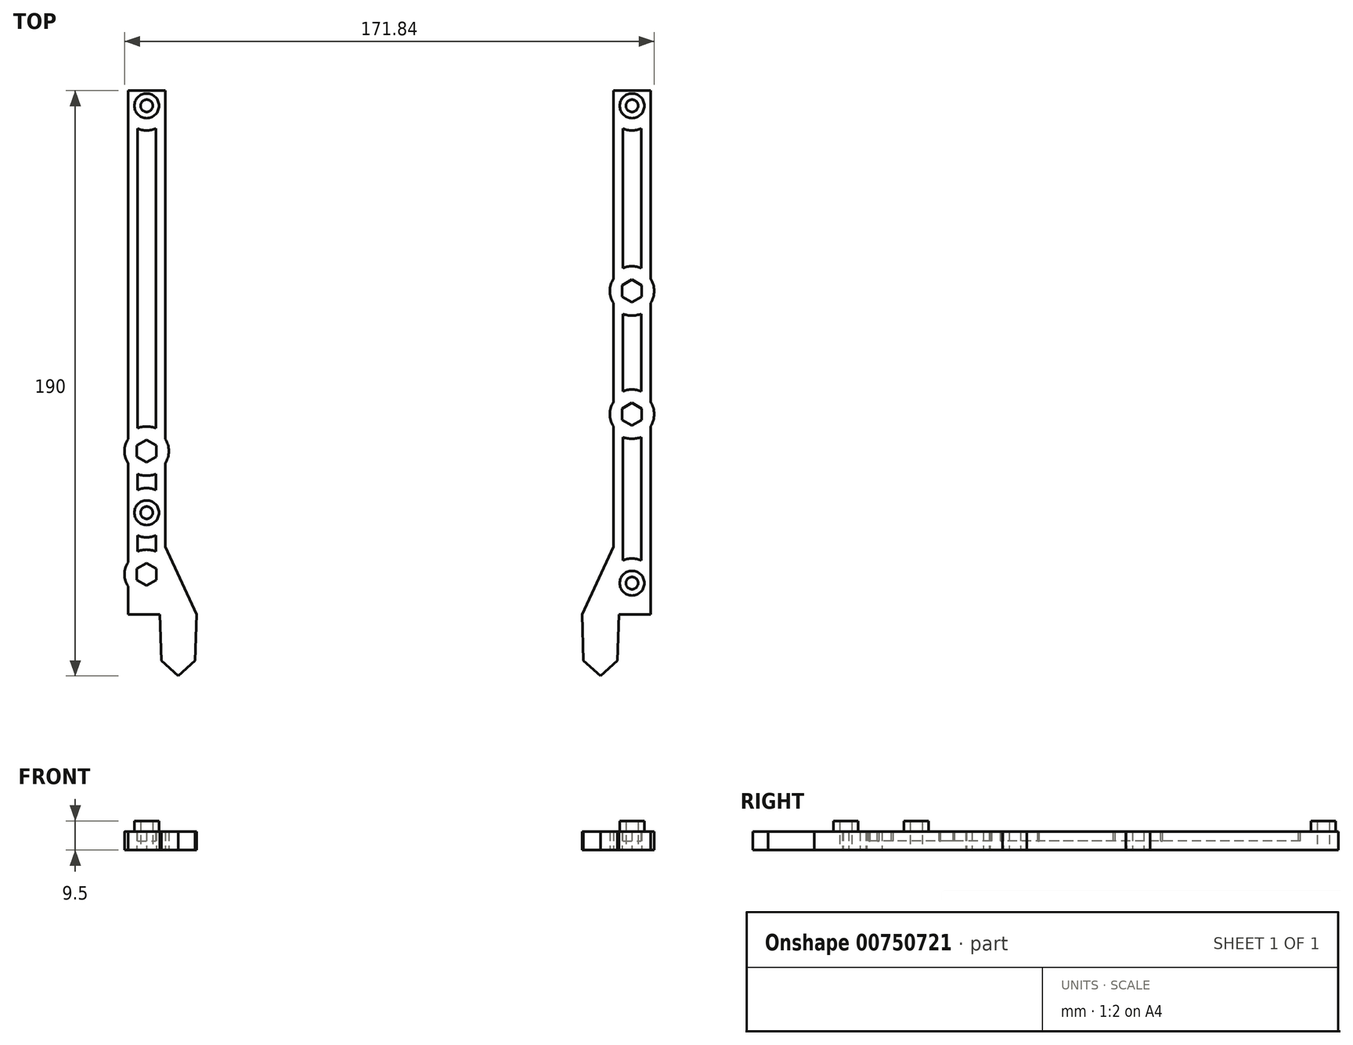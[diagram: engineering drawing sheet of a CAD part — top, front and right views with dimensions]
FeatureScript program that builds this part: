
annotation { "Feature Type Name" : "Feature", "Feature Type Description" : "" }
export const myFeature = defineFeature(function(context is Context, id is Id, definition is map)
    precondition{}
    {
        {
            var Q0;
            Q0=qCreatedBy(makeId("Top.planeOp"),FACE);
            var sketch = newSketch(context, id + "F0", { "sketchPlane" : qUnion([Q0])});
            skLineSegment(sketch, "E0", {"start": v(-84.74, -85) * mm, "end": v(-84.74, 85) * mm});
            skLineSegment(sketch, "E1", {"start": v(-84.74, 85) * mm, "end": v(-72.74, 85) * mm});
            skLineSegment(sketch, "E2", {"start": v(-72.74, 85) * mm, "end": v(-72.74, -63.04) * mm});
            skLineSegment(sketch, "E3", {"start": v(-74.5, -85) * mm, "end": v(-84.74, -85) * mm});
            skLineSegment(sketch, "E4", {"start": v(-74.5, -85) * mm, "end": v(-62.5, -85) * mm, "construction": true});
            skLineSegment(sketch, "E5", {"start": v(-72.74, -63.04) * mm, "end": v(-62.5, -85) * mm});
            skLineSegment(sketch, "E6", {"start": v(-74.5, -85) * mm, "end": v(-74, -100) * mm});
            skLineSegment(sketch, "E7", {"start": v(-74, -100) * mm, "end": v(-68.5, -105) * mm});
            skLineSegment(sketch, "E8", {"start": v(-68.5, -105) * mm, "end": v(-63, -100) * mm});
            skLineSegment(sketch, "E9", {"start": v(-63, -100) * mm, "end": v(-62.5, -85) * mm});
            skLineSegment(sketch, "E10", {"start": v(-78.74, 85) * mm, "end": v(-78.74, -85) * mm, "construction": true});
            skLineSegment(sketch, "E11.MirrorCS", {"start": v(68.5, -105) * mm, "end": v(63, -100) * mm});
            skLineSegment(sketch, "E12.MirrorCS", {"start": v(74, -100) * mm, "end": v(68.5, -105) * mm});
            skLineSegment(sketch, "E13.MirrorCS", {"start": v(74.5, -85) * mm, "end": v(84.74, -85) * mm});
            skLineSegment(sketch, "E14.MirrorCS", {"start": v(84.74, 85) * mm, "end": v(72.74, 85) * mm});
            skLineSegment(sketch, "E15.MirrorCS", {"start": v(74.5, -85) * mm, "end": v(74, -100) * mm});
            skLineSegment(sketch, "E16.MirrorCS", {"start": v(78.74, 85) * mm, "end": v(78.74, -85) * mm, "construction": true});
            skLineSegment(sketch, "E17.MirrorCS", {"start": v(84.74, -85) * mm, "end": v(84.74, 85) * mm});
            skLineSegment(sketch, "E18.MirrorCS", {"start": v(72.74, -63.04) * mm, "end": v(62.5, -85) * mm});
            skLineSegment(sketch, "E19.MirrorCS", {"start": v(74.5, -85) * mm, "end": v(62.5, -85) * mm, "construction": true});
            skLineSegment(sketch, "E20.MirrorCS", {"start": v(72.74, 85) * mm, "end": v(72.74, -63.04) * mm});
            skLineSegment(sketch, "E21.MirrorCS", {"start": v(63, -100) * mm, "end": v(62.5, -85) * mm});
            skCircle(sketch, "E22", {"center": v(-78.74, 80.1) * mm, "radius": 2 * mm});
            skCircle(sketch, "E23", {"center": v(-78.74, -51.98) * mm, "radius": 2 * mm});
            skCircle(sketch, "E24", {"center": v(78.74, 80.1) * mm, "radius": 2 * mm});
            skCircle(sketch, "E25", {"center": v(78.74, -74.84) * mm, "radius": 2 * mm});
            skLineSegment(sketch, "E26", {"start": v(-78.74, 80.1) * mm, "end": v(78.74, 80.1) * mm, "construction": true});
            skLineSegment(sketch, "E27", {"start": v(-78.74, 0) * mm, "end": v(78.74, 0) * mm, "construction": true});
            skPoint(sketch, "E28", {"position": v(0, 0) * mm});
            skLineSegment(sketch, "E29", {"start": v(-68.5, -85) * mm, "end": v(68.5, -85) * mm, "construction": true});
            skSolve(sketch);
        }
        {
            var Q0;
            Q0 = qSketchRegion(id + "F0", true);
            extrude(context, id + "F1", {"entities" : qUnion([Q0]), "depth" : 6 * mm, "offsetDistance" : 25 * mm});
        }
        {
            var Q0;
            Q0=qCreatedBy(makeId("Top.planeOp"),FACE);
            var sketch = newSketch(context, id + "F2", { "sketchPlane" : qUnion([Q0])});
            skCircle(sketch, "E30.0", {"center": v(-78.74, -51.98) * mm, "radius": 2 * mm});
            skCircle(sketch, "E30.1", {"center": v(78.74, -74.84) * mm, "radius": 2 * mm});
            skCircle(sketch, "E30.2", {"center": v(78.74, 80.1) * mm, "radius": 2 * mm});
            skCircle(sketch, "E30.3", {"center": v(-78.74, 80.1) * mm, "radius": 2 * mm});
            skCircle(sketch, "E31", {"center": v(-78.74, -51.98) * mm, "radius": 4 * mm});
            skCircle(sketch, "E32", {"center": v(-78.74, 80.1) * mm, "radius": 4 * mm});
            skCircle(sketch, "E33", {"center": v(78.74, -74.84) * mm, "radius": 4 * mm});
            skCircle(sketch, "E34", {"center": v(78.74, 80.1) * mm, "radius": 4 * mm});
            skSolve(sketch);
        }
        {
            var Q0;
            Q0 = qSketchRegion(id + "F2", true);
            extrude(context, id + "F3", {"entities" : qUnion([Q0]), "operationType" : NewBodyOperationType.ADD, "depth" : 9.5 * mm, "offsetDistance" : 25 * mm});
        }
        {
            var Q0;
            Q0=qCreatedBy(makeId("Top.planeOp"),FACE);
            var sketch = newSketch(context, id + "F4", { "sketchPlane" : qUnion([Q0])});
            skLineSegment(sketch, "E35", {"start": v(-78.74, -31.98) * mm, "end": v(-78.74, -71.98) * mm, "construction": true});
            skLineSegment(sketch, "E36", {"start": v(78.74, 20) * mm, "end": v(78.74, -20) * mm, "construction": true});
            skPoint(sketch, "E37", {"position": v(-78.74, -51.98) * mm});
            skPoint(sketch, "E38", {"position": v(78.74, 0) * mm});
            skCircle(sketch, "E39", {"center": v(-78.74, -31.98) * mm, "radius": 7.17 * mm});
            skCircle(sketch, "E40", {"center": v(-78.74, -71.98) * mm, "radius": 7.17 * mm});
            skCircle(sketch, "E41", {"center": v(78.74, 20) * mm, "radius": 7.17 * mm});
            skCircle(sketch, "E42", {"center": v(78.74, -20) * mm, "radius": 7.17 * mm});
            skCircle(sketch, "E43.cCircle", {"center": v(78.74, 20) * mm, "radius": 3.17 * mm, "construction": true});
            skLineSegment(sketch, "E43.0", {"start": v(81.92, 21.83) * mm, "end": v(81.92, 18.17) * mm});
            skLineSegment(sketch, "E43.1", {"start": v(81.92, 18.17) * mm, "end": v(78.74, 16.33) * mm});
            skLineSegment(sketch, "E43.2", {"start": v(78.74, 16.33) * mm, "end": v(75.57, 18.17) * mm});
            skLineSegment(sketch, "E43.3", {"start": v(75.56, 18.17) * mm, "end": v(75.56, 21.83) * mm});
            skLineSegment(sketch, "E43.4", {"start": v(75.56, 21.83) * mm, "end": v(78.74, 23.67) * mm});
            skLineSegment(sketch, "E43.5", {"start": v(78.74, 23.67) * mm, "end": v(81.92, 21.83) * mm});
            skPoint(sketch, "E43.0.midPoint", {"position": v(81.92, 20) * mm});
            skCircle(sketch, "E44.cCircle", {"center": v(78.74, -20) * mm, "radius": 3.17 * mm, "construction": true});
            skLineSegment(sketch, "E44.0", {"start": v(81.91, -18.17) * mm, "end": v(81.91, -21.83) * mm});
            skLineSegment(sketch, "E44.1", {"start": v(81.91, -21.83) * mm, "end": v(78.74, -23.67) * mm});
            skLineSegment(sketch, "E44.2", {"start": v(78.74, -23.67) * mm, "end": v(75.56, -21.83) * mm});
            skLineSegment(sketch, "E44.3", {"start": v(75.56, -21.83) * mm, "end": v(75.56, -18.17) * mm});
            skLineSegment(sketch, "E44.4", {"start": v(75.56, -18.17) * mm, "end": v(78.74, -16.33) * mm});
            skLineSegment(sketch, "E44.5", {"start": v(78.74, -16.33) * mm, "end": v(81.91, -18.17) * mm});
            skPoint(sketch, "E44.0.midPoint", {"position": v(81.91, -20) * mm});
            skCircle(sketch, "E45.cCircle", {"center": v(-78.74, -31.98) * mm, "radius": 3.17 * mm, "construction": true});
            skLineSegment(sketch, "E45.0", {"start": v(-75.57, -30.15) * mm, "end": v(-75.57, -33.81) * mm});
            skLineSegment(sketch, "E45.1", {"start": v(-75.57, -33.81) * mm, "end": v(-78.74, -35.65) * mm});
            skLineSegment(sketch, "E45.2", {"start": v(-78.74, -35.65) * mm, "end": v(-81.92, -33.81) * mm});
            skLineSegment(sketch, "E45.3", {"start": v(-81.92, -33.81) * mm, "end": v(-81.92, -30.15) * mm});
            skLineSegment(sketch, "E45.4", {"start": v(-81.92, -30.15) * mm, "end": v(-78.74, -28.31) * mm});
            skLineSegment(sketch, "E45.5", {"start": v(-78.74, -28.31) * mm, "end": v(-75.57, -30.15) * mm});
            skPoint(sketch, "E45.0.midPoint", {"position": v(-75.57, -31.98) * mm});
            skCircle(sketch, "E46.cCircle", {"center": v(-78.74, -71.98) * mm, "radius": 3.17 * mm, "construction": true});
            skLineSegment(sketch, "E46.0", {"start": v(-75.57, -70.15) * mm, "end": v(-75.57, -73.81) * mm});
            skLineSegment(sketch, "E46.1", {"start": v(-75.57, -73.81) * mm, "end": v(-78.74, -75.65) * mm});
            skLineSegment(sketch, "E46.2", {"start": v(-78.74, -75.65) * mm, "end": v(-81.92, -73.81) * mm});
            skLineSegment(sketch, "E46.3", {"start": v(-81.92, -73.81) * mm, "end": v(-81.92, -70.15) * mm});
            skLineSegment(sketch, "E46.4", {"start": v(-81.92, -70.15) * mm, "end": v(-78.74, -68.31) * mm});
            skLineSegment(sketch, "E46.5", {"start": v(-78.74, -68.31) * mm, "end": v(-75.57, -70.15) * mm});
            skPoint(sketch, "E46.0.midPoint", {"position": v(-75.57, -71.98) * mm});
            skCircle(sketch, "E47.0", {"center": v(-78.74, -51.98) * mm, "radius": 2 * mm, "construction": true});
            skLineSegment(sketch, "E48.0", {"start": v(78.74, 85) * mm, "end": v(78.74, -85) * mm, "construction": true});
            skSolve(sketch);
        }
        {
            var Q0;
            Q0 = qSketchRegion(id + "F4", true);
            var Q1;
            Q1=makeQuery(id+"F1.opExtrude","CAP_FACE",FACE,{"disambiguationData":[OSD([sQuery(id+"F0.wireOp",EDGE,"E0"),sQuery(id+"F0.wireOp",EDGE,"E1"),sQuery(id+"F0.wireOp",EDGE,"E2"),sQuery(id+"F0.wireOp",EDGE,"E3"),sQuery(id+"F0.wireOp",EDGE,"E5"),sQuery(id+"F0.wireOp",EDGE,"E6"),sQuery(id+"F0.wireOp",EDGE,"E7"),sQuery(id+"F0.wireOp",EDGE,"E8"),sQuery(id+"F0.wireOp",EDGE,"E9"),sQuery(id+"F0.wireOp",EDGE,"E22"),sQuery(id+"F0.wireOp",EDGE,"E23")])],"isStart":false});
            extrude(context, id + "F5", {"entities" : qUnion([Q0]), "operationType" : NewBodyOperationType.ADD, "endBound" : BoundingType.UP_TO_SURFACE, "depth" : 25 * mm, "endBoundEntityFace" : qUnion([Q1]), "offsetDistance" : 25 * mm});
        }
        {
            var Q0;
            Q0=makeQuery(id+"F4.imprint","IMPRINT",FACE,{"disambiguationData":[TD([[makeQuery(id+"F4.imprint","IMPRINT",EDGE,{"derivedFrom":sQuery(id+"F4.wireOp",EDGE,"E45.0")}),-1.0]])]});
            var Q1;
            Q1=makeQuery(id+"F4.imprint","IMPRINT",FACE,{"disambiguationData":[TD([[makeQuery(id+"F4.imprint","IMPRINT",EDGE,{"derivedFrom":sQuery(id+"F4.wireOp",EDGE,"E46.0")}),-1.0]])]});
            var Q2;
            Q2=makeQuery(id+"F4.imprint","IMPRINT",FACE,{"disambiguationData":[TD([[makeQuery(id+"F4.imprint","IMPRINT",EDGE,{"derivedFrom":sQuery(id+"F4.wireOp",EDGE,"E44.0")}),-1.0]])]});
            var Q3;
            Q3=makeQuery(id+"F4.imprint","IMPRINT",FACE,{"disambiguationData":[TD([[makeQuery(id+"F4.imprint","IMPRINT",EDGE,{"derivedFrom":sQuery(id+"F4.wireOp",EDGE,"E43.0")}),-1.0]])]});
            extrude(context, id + "F6", {"entities" : qUnion([Q0, Q1, Q2, Q3]), "operationType" : NewBodyOperationType.REMOVE, "endBound" : BoundingType.THROUGH_ALL, "depth" : 25 * mm, "offsetDistance" : 25 * mm});
        }
        {
            var Q0;
            Q0=makeQuery(id+"F5.boolean.opBoolean","MERGE",FACE,{"derivedFrom":[makeQuery(id+"F1.opExtrude","CAP_FACE",FACE,{"disambiguationData":[OSD([sQuery(id+"F0.wireOp",EDGE,"E0"),sQuery(id+"F0.wireOp",EDGE,"E1"),sQuery(id+"F0.wireOp",EDGE,"E2"),sQuery(id+"F0.wireOp",EDGE,"E3"),sQuery(id+"F0.wireOp",EDGE,"E5"),sQuery(id+"F0.wireOp",EDGE,"E6"),sQuery(id+"F0.wireOp",EDGE,"E7"),sQuery(id+"F0.wireOp",EDGE,"E8"),sQuery(id+"F0.wireOp",EDGE,"E9"),sQuery(id+"F0.wireOp",EDGE,"E22"),sQuery(id+"F0.wireOp",EDGE,"E23")])],"isStart":false}),makeQuery(id+"F5.opExtrude","CAP_FACE",FACE,{"disambiguationData":[OSD([sQuery(id+"F4.wireOp",EDGE,"SRqQKz3n-vC3j-pEua-mdw7-BWJlVyXjlK89"),sQuery(id+"F4.wireOp",EDGE,"6ef7abd1-16c0-451d-831a-03148b24f05d.0"),sQuery(id+"F4.wireOp",EDGE,"6ef7abd1-16c0-451d-831a-03148b24f05d.1"),sQuery(id+"F4.wireOp",EDGE,"6ef7abd1-16c0-451d-831a-03148b24f05d.2"),sQuery(id+"F4.wireOp",EDGE,"6ef7abd1-16c0-451d-831a-03148b24f05d.3"),sQuery(id+"F4.wireOp",EDGE,"6ef7abd1-16c0-451d-831a-03148b24f05d.4"),sQuery(id+"F4.wireOp",EDGE,"6ef7abd1-16c0-451d-831a-03148b24f05d.5")])],"isStart":false}),makeQuery(id+"F5.opExtrude","CAP_FACE",FACE,{"disambiguationData":[OSD([sQuery(id+"F4.wireOp",EDGE,"ubodkBIp-3K7r-hwd0-fg8X-iVVL0fXusPFp"),sQuery(id+"F4.wireOp",EDGE,"432d3784-bb52-43d7-afc3-5c8ebb29258b.0"),sQuery(id+"F4.wireOp",EDGE,"432d3784-bb52-43d7-afc3-5c8ebb29258b.1"),sQuery(id+"F4.wireOp",EDGE,"432d3784-bb52-43d7-afc3-5c8ebb29258b.2"),sQuery(id+"F4.wireOp",EDGE,"432d3784-bb52-43d7-afc3-5c8ebb29258b.3"),sQuery(id+"F4.wireOp",EDGE,"432d3784-bb52-43d7-afc3-5c8ebb29258b.4"),sQuery(id+"F4.wireOp",EDGE,"432d3784-bb52-43d7-afc3-5c8ebb29258b.5")])],"isStart":false})]});
            var sketch = newSketch(context, id + "F7", { "sketchPlane" : qUnion([Q0])});
            skCircle(sketch, "E49.0", {"center": v(78.74, 80.1) * mm, "radius": 2 * mm, "construction": true});
            skCircle(sketch, "E50.0", {"center": v(78.74, -74.84) * mm, "radius": 2 * mm, "construction": true});
            skCircle(sketch, "E50.1", {"center": v(78.74, -20) * mm, "radius": 3.17 * mm, "construction": true});
            skCircle(sketch, "E50.2", {"center": v(78.74, 20) * mm, "radius": 3.17 * mm, "construction": true});
            skCircle(sketch, "E50.3", {"center": v(-78.74, 80.1) * mm, "radius": 2 * mm, "construction": true});
            skCircle(sketch, "E50.4", {"center": v(-78.74, -31.98) * mm, "radius": 3.17 * mm, "construction": true});
            skCircle(sketch, "E50.5", {"center": v(-78.74, -51.98) * mm, "radius": 2 * mm, "construction": true});
            skCircle(sketch, "E50.6", {"center": v(-78.74, -71.98) * mm, "radius": 3.17 * mm, "construction": true});
            skArc(sketch, "E51", {"start": v(-81.74, -39.4) * mm, "mid": v(-78.74, -39.98) * mm, "end": v(-75.74, -39.4) * mm});
            skArc(sketch, "E52", {"start": v(-75.74, -44.56) * mm, "mid": v(-78.74, -43.98) * mm, "end": v(-81.74, -44.56) * mm});
            skArc(sketch, "E53", {"start": v(81.74, -12.58) * mm, "mid": v(78.74, -12) * mm, "end": v(75.74, -12.58) * mm});
            skArc(sketch, "E54", {"start": v(75.74, 12.58) * mm, "mid": v(78.74, 12) * mm, "end": v(81.74, 12.58) * mm});
            skLineSegment(sketch, "E55", {"start": v(-81.74, 72.68) * mm, "end": v(-81.74, -24.56) * mm});
            skLineSegment(sketch, "E56", {"start": v(-75.74, 72.68) * mm, "end": v(-75.74, -24.56) * mm});
            skLineSegment(sketch, "E57", {"start": v(-81.74, 72.68) * mm, "end": v(-81.74, 72.68) * mm});
            skLineSegment(sketch, "E58", {"start": v(-81.74, 72.68) * mm, "end": v(-75.74, 72.68) * mm, "construction": true});
            skArc(sketch, "E59", {"start": v(-75.74, 72.68) * mm, "mid": v(-78.74, 88.1) * mm, "end": v(-81.74, 72.68) * mm, "construction": true});
            skArc(sketch, "E60", {"start": v(-81.74, 72.68) * mm, "mid": v(-78.74, 72.1) * mm, "end": v(-75.74, 72.68) * mm});
            skArc(sketch, "E61.trimOffspring", {"start": v(-75.74, -24.56) * mm, "mid": v(-78.74, -23.98) * mm, "end": v(-81.74, -24.56) * mm});
            skArc(sketch, "E62.trimOffspring", {"start": v(-81.74, -59.4) * mm, "mid": v(-78.74, -59.98) * mm, "end": v(-75.74, -59.4) * mm});
            skArc(sketch, "E63", {"start": v(-81.74, -64.56) * mm, "mid": v(-78.74, -79.98) * mm, "end": v(-75.74, -64.56) * mm, "construction": true});
            skArc(sketch, "E64", {"start": v(-75.74, -64.56) * mm, "mid": v(-78.74, -63.98) * mm, "end": v(-81.74, -64.56) * mm});
            skLineSegment(sketch, "E65", {"start": v(-75.74, -59.4) * mm, "end": v(-75.74, -64.56) * mm});
            skLineSegment(sketch, "E66", {"start": v(-75.74, -44.56) * mm, "end": v(-75.74, -59.4) * mm, "construction": true});
            skLineSegment(sketch, "E67", {"start": v(-81.74, -44.56) * mm, "end": v(-81.74, -44.56) * mm});
            skLineSegment(sketch, "E68", {"start": v(-81.74, -59.4) * mm, "end": v(-81.74, -64.56) * mm});
            skLineSegment(sketch, "E69", {"start": v(-81.74, -39.4) * mm, "end": v(-81.74, -44.56) * mm});
            skLineSegment(sketch, "E70", {"start": v(-81.74, -24.56) * mm, "end": v(-81.74, -39.4) * mm, "construction": true});
            skLineSegment(sketch, "E71", {"start": v(-75.74, -24.56) * mm, "end": v(-75.74, -39.4) * mm, "construction": true});
            skLineSegment(sketch, "E72", {"start": v(-75.74, -39.4) * mm, "end": v(-75.74, -44.56) * mm});
            skLineSegment(sketch, "E73", {"start": v(-81.74, -44.56) * mm, "end": v(-81.74, -59.4) * mm, "construction": true});
            skLineSegment(sketch, "E74", {"start": v(75.74, 72.68) * mm, "end": v(75.74, 27.42) * mm});
            skLineSegment(sketch, "E75", {"start": v(81.74, 72.68) * mm, "end": v(81.74, 27.42) * mm});
            skLineSegment(sketch, "E76", {"start": v(81.74, 72.68) * mm, "end": v(75.74, 72.68) * mm, "construction": true});
            skArc(sketch, "E77", {"start": v(75.74, 72.68) * mm, "mid": v(78.74, 72.1) * mm, "end": v(81.74, 72.68) * mm});
            skArc(sketch, "E78", {"start": v(81.74, 72.68) * mm, "mid": v(78.74, 88.1) * mm, "end": v(75.74, 72.68) * mm, "construction": true});
            skLineSegment(sketch, "E79", {"start": v(81.74, -67.42) * mm, "end": v(81.74, -67.42) * mm});
            skArc(sketch, "E80", {"start": v(81.74, -67.42) * mm, "mid": v(78.74, -66.84) * mm, "end": v(75.74, -67.42) * mm});
            skArc(sketch, "E81", {"start": v(75.74, -67.42) * mm, "mid": v(78.74, -82.84) * mm, "end": v(81.74, -67.42) * mm, "construction": true});
            skArc(sketch, "E82.trimOffspring", {"start": v(81.74, 27.42) * mm, "mid": v(78.74, 28) * mm, "end": v(75.74, 27.42) * mm});
            skArc(sketch, "E83.trimOffspring", {"start": v(75.74, -27.42) * mm, "mid": v(78.74, -28) * mm, "end": v(81.74, -27.42) * mm});
            skLineSegment(sketch, "E84", {"start": v(75.74, 27.42) * mm, "end": v(75.74, 12.58) * mm, "construction": true});
            skLineSegment(sketch, "E85", {"start": v(81.74, 27.42) * mm, "end": v(81.74, 12.58) * mm, "construction": true});
            skLineSegment(sketch, "E86", {"start": v(81.74, 12.58) * mm, "end": v(81.74, -12.58) * mm});
            skLineSegment(sketch, "E87", {"start": v(75.74, 12.58) * mm, "end": v(75.74, -12.58) * mm});
            skLineSegment(sketch, "E88", {"start": v(75.74, -12.58) * mm, "end": v(75.74, -27.42) * mm, "construction": true});
            skLineSegment(sketch, "E89", {"start": v(75.74, -27.42) * mm, "end": v(75.74, -67.42) * mm});
            skLineSegment(sketch, "E90", {"start": v(81.74, -12.58) * mm, "end": v(81.74, -27.42) * mm, "construction": true});
            skLineSegment(sketch, "E91", {"start": v(81.74, -27.42) * mm, "end": v(81.74, -67.42) * mm});
            skSolve(sketch);
        }
        {
            var Q0;
            Q0 = qSketchRegion(id + "F7", true);
            extrude(context, id + "F8", {"entities" : qUnion([Q0]), "operationType" : NewBodyOperationType.REMOVE, "oppositeDirection" : true, "depth" : 3 * mm, "offsetDistance" : 25 * mm});
        }
    });
